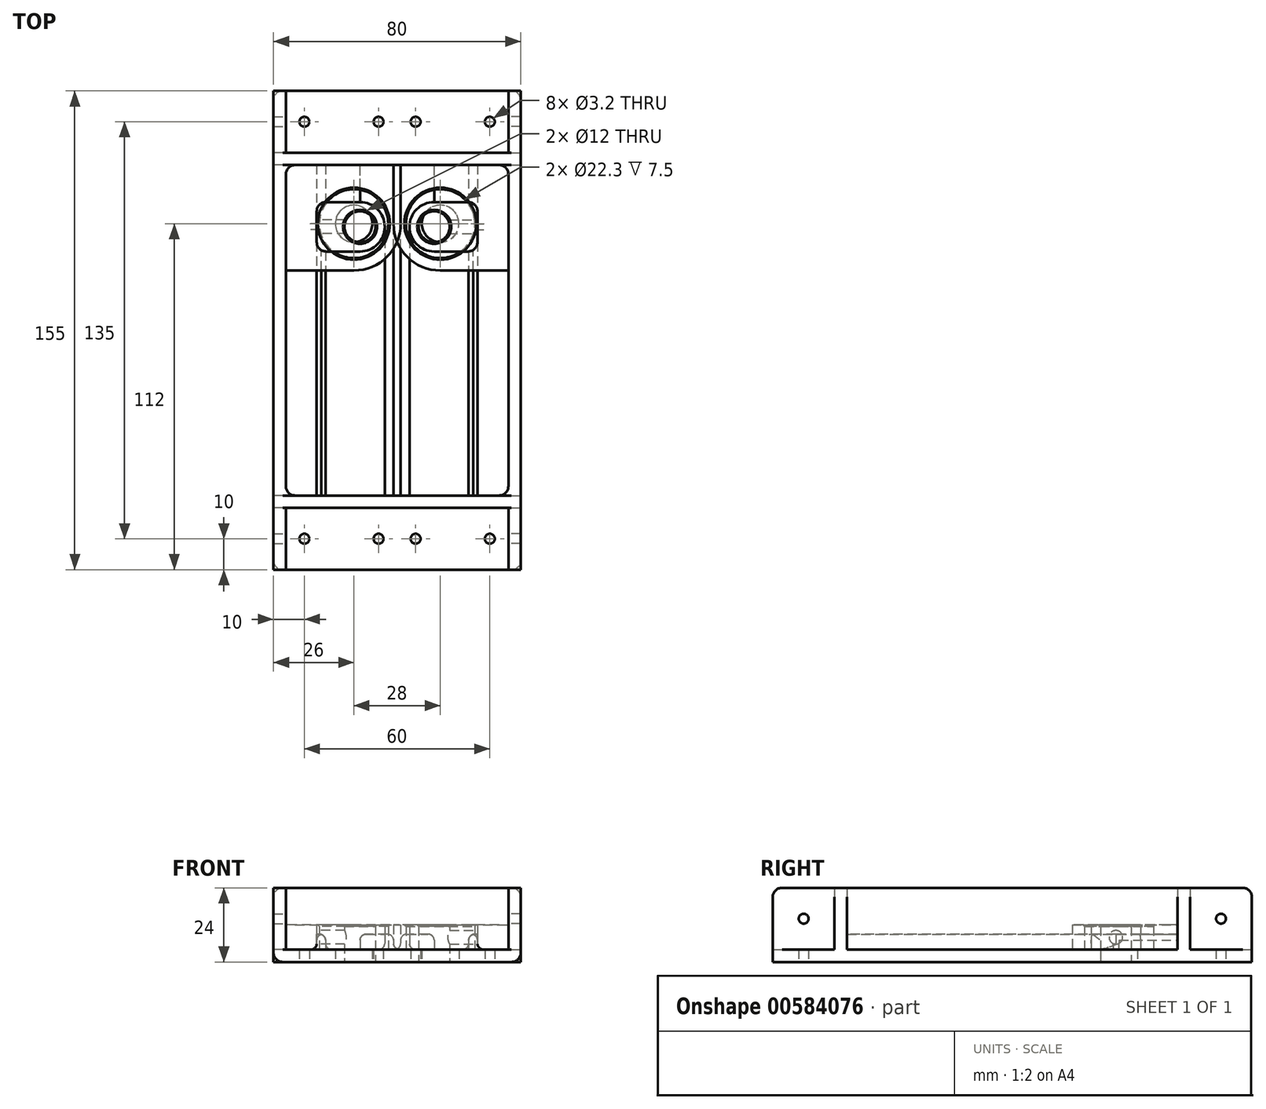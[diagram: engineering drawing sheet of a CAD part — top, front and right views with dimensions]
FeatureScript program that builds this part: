
annotation { "Feature Type Name" : "Feature", "Feature Type Description" : "" }
export const myFeature = defineFeature(function(context is Context, id is Id, definition is map)
    precondition{}
    {
        {
            var Q0;
            Q0=qCreatedBy(makeId("Top.planeOp"),FACE);
            var sketch = newSketch(context, id + "F0", { "sketchPlane" : qUnion([Q0])});
            skLineSegment(sketch, "E0.bottom", {"start": v(40, -77.5) * mm, "end": v(-40, -77.5) * mm});
            skLineSegment(sketch, "E0.top", {"start": v(40, 77.5) * mm, "end": v(-40, 77.5) * mm});
            skLineSegment(sketch, "E0.left", {"start": v(40, -77.5) * mm, "end": v(40, 77.5) * mm});
            skLineSegment(sketch, "E0.right", {"start": v(-40, -77.5) * mm, "end": v(-40, 77.5) * mm});
            skPoint(sketch, "E0.middle", {"position": v(0, 0) * mm});
            skLineSegment(sketch, "E1", {"start": v(-36, 77.5) * mm, "end": v(-36, 57.5) * mm});
            skLineSegment(sketch, "E2", {"start": v(-36, -53.5) * mm, "end": v(40, -53.5) * mm});
            skLineSegment(sketch, "E3", {"start": v(-36, -57.5) * mm, "end": v(40, -57.5) * mm});
            skLineSegment(sketch, "E4", {"start": v(-36, 57.5) * mm, "end": v(40, 57.5) * mm});
            skLineSegment(sketch, "E5", {"start": v(-36, 53.5) * mm, "end": v(40, 53.5) * mm});
            skLineSegment(sketch, "E6.trimOffspring", {"start": v(-36, 53.5) * mm, "end": v(-36, -53.5) * mm});
            skLineSegment(sketch, "E7.trimOffspring", {"start": v(-36, -57.5) * mm, "end": v(-36, -77.5) * mm});
            skCircle(sketch, "E8", {"center": v(-6, 67.5) * mm, "radius": 1.6 * mm});
            skCircle(sketch, "E9", {"center": v(30, 67.5) * mm, "radius": 1.6 * mm});
            skCircle(sketch, "E10", {"center": v(-6, -67.5) * mm, "radius": 1.6 * mm});
            skCircle(sketch, "E11", {"center": v(30, -67.5) * mm, "radius": 1.6 * mm});
            skCircle(sketch, "E12", {"center": v(-14, 34.5) * mm, "radius": 4 * mm, "construction": true});
            skCircle(sketch, "E13", {"center": v(12, 33.5) * mm, "radius": 5 * mm});
            skCircle(sketch, "E14.0", {"center": v(-14, 34.5) * mm, "radius": 6 * mm});
            skSolve(sketch);
        }
        {
            var Q0;
            {var subQ1=sQuery(id+"F0.wireOp",EDGE,"E3");Q0=makeQuery(id+"F0.imprint","IMPRINT",FACE,{"disambiguationData":[TD([[makeQuery(id+"F0.imprint","IMPRINT",EDGE,{"derivedFrom":subQ1}),-1.0]])]});}
            var Q1;
            {var subQ1=sQuery(id+"F0.wireOp",EDGE,"E2");Q1=makeQuery(id+"F0.imprint","IMPRINT",FACE,{"disambiguationData":[TD([[makeQuery(id+"F0.imprint","IMPRINT",EDGE,{"derivedFrom":subQ1}),1.0]])]});}
            var Q2;
            {var subQ0=sQuery(id+"F0.wireOp",EDGE,"E1");Q2=makeQuery(id+"F0.imprint","IMPRINT",FACE,{"disambiguationData":[TD([[makeQuery(id+"F0.imprint","IMPRINT",EDGE,{"derivedFrom":subQ0}),1.0]])]});}
            extrude(context, id + "F1", {"entities" : qUnion([Q0, Q1, Q2]), "depth" : 4 * mm, "offsetDistance" : 25 * mm});
        }
        {
            var Q0;
            {var subQ3=sQuery(id+"F0.wireOp",EDGE,"E0.right");Q0=makeQuery(id+"F0.imprint","IMPRINT",FACE,{"disambiguationData":[TD([[makeQuery(id+"F0.imprint","IMPRINT",EDGE,{"derivedFrom":subQ3}),-1.0]])]});}
            extrude(context, id + "F2", {"entities" : qUnion([Q0]), "operationType" : NewBodyOperationType.ADD, "depth" : 24 * mm, "offsetDistance" : 25 * mm});
        }
        {
            var Q0;
            Q0=makeQuery(id+"F1.opExtrude","CAP_FACE",FACE,{"disambiguationData":[OSD([sQuery(id+"F0.wireOp",EDGE,"E0.left"),sQuery(id+"F0.wireOp",EDGE,"E2"),sQuery(id+"F0.wireOp",EDGE,"E5"),sQuery(id+"F0.wireOp",EDGE,"E6.trimOffspring"),sQuery(id+"F0.wireOp",EDGE,"E13"),sQuery(id+"F0.wireOp",EDGE,"E14.0")])],"isStart":false});
            var sketch = newSketch(context, id + "F3", { "sketchPlane" : qUnion([Q0])});
            skCircle(sketch, "E15", {"center": v(-14, 34.5) * mm, "radius": 11.15 * mm});
            skCircle(sketch, "E16", {"center": v(-14, 34.5) * mm, "radius": 15.15 * mm});
            skCircle(sketch, "E17.0", {"center": v(12, 33.5) * mm, "radius": 8 * mm});
            skLineSegment(sketch, "E18", {"start": v(12, 41.5) * mm, "end": v(26, 41.5) * mm});
            skLineSegment(sketch, "E19", {"start": v(12, 25.5) * mm, "end": v(26, 25.5) * mm});
            skLineSegment(sketch, "E20", {"start": v(26, 41.5) * mm, "end": v(26, 25.5) * mm});
            skLineSegment(sketch, "E21", {"start": v(1.15, 34.5) * mm, "end": v(1.15, 53.5) * mm});
            skLineSegment(sketch, "E22", {"start": v(-14, 19.35) * mm, "end": v(-36, 19.35) * mm});
            skSolve(sketch);
        }
        {
            var Q0;
            Q0=makeQuery(id+"F3.imprint","IMPRINT",FACE,{"disambiguationData":[TD([[makeQuery(id+"F3.imprint","IMPRINT",EDGE,{"derivedFrom":sQuery(id+"F3.wireOp",EDGE,"E15")}),-1.0]])]});
            var Q1;
            {var subQ0=sQuery(id+"F3.wireOp",EDGE,"E21");Q1=makeQuery(id+"F3.imprint","IMPRINT",FACE,{"disambiguationData":[TD([[makeQuery(id+"F3.imprint","IMPRINT",EDGE,{"derivedFrom":subQ0}),1.0]])]});}
            var Q2;
            {var subQ0=sQuery(id+"F3.wireOp",EDGE,"E22");Q2=makeQuery(id+"F3.imprint","IMPRINT",FACE,{"disambiguationData":[TD([[makeQuery(id+"F3.imprint","IMPRINT",EDGE,{"derivedFrom":subQ0}),-1.0]])]});}
            var Q3;
            {var subQ0=sQuery(id+"F3.wireOp",EDGE,"E18");Q3=makeQuery(id+"F3.imprint","IMPRINT",FACE,{"disambiguationData":[TD([[makeQuery(id+"F3.imprint","IMPRINT",EDGE,{"derivedFrom":subQ0}),-1.0]])]});}
            var Q4;
            Q4=makeQuery(id+"F3.imprint","IMPRINT",FACE,{"disambiguationData":[TD([[makeQuery(id+"F3.imprint","IMPRINT",EDGE,{"derivedFrom":makeQuery(id+"F1.opExtrude","CAP_EDGE",EDGE,{"disambiguationData":[OSD([sQuery(id+"F0.wireOp",EDGE,"E13")])],"isStart":false})}),-1.0]])]});
            var Q5;
            {var subQ0=sQuery(id+"F3.wireOp",EDGE,"E16");var subQ1=makeQuery(id+"F1.opExtrude","CAP_EDGE",EDGE,{"disambiguationData":[OSD([sQuery(id+"F0.wireOp",EDGE,"E5")])],"isStart":false});var subQ2=makeQuery(id+"F3.imprint","INTERSECT",VERTEX,{"disambiguationData":[OD(1.0)],"derivedFrom":[subQ1,subQ0]});Q5=makeQuery(id+"F3.imprint","IMPRINT",FACE,{"disambiguationData":[TD([[makeQuery(id+"F3.imprint","IMPRINT",EDGE,{"disambiguationData":[TD([[subQ2,-1.0]])],"derivedFrom":subQ0}),-1.0]])]});}
            extrude(context, id + "F4", {"entities" : qUnion([Q0, Q1, Q2, Q3, Q4, Q5]), "operationType" : NewBodyOperationType.ADD, "depth" : 8 * mm, "offsetDistance" : 25 * mm});
        }
        {
            var Q0;
            Q0=makeQuery(id+"F2.opExtrude","SWEPT_FACE",FACE,{"disambiguationData":[OSD([sQuery(id+"F0.wireOp",EDGE,"E1")])]});
            var sketch = newSketch(context, id + "F5", { "sketchPlane" : qUnion([Q0])});
            skLineSegment(sketch, "E23.0.0", {"start": v(-77.5, 4) * mm, "end": v(-57.5, 4) * mm});
            skLineSegment(sketch, "E23.0.1", {"start": v(-57.5, 4) * mm, "end": v(-57.5, 24) * mm});
            skLineSegment(sketch, "E23.0.2", {"start": v(-57.5, 24) * mm, "end": v(-77.5, 24) * mm});
            skLineSegment(sketch, "E23.0.3", {"start": v(-77.5, 24) * mm, "end": v(-77.5, 4) * mm});
            skCircle(sketch, "E24", {"center": v(67.5, 14) * mm, "radius": 1.6 * mm});
            skPoint(sketch, "E24.centerSnap0", {"position": v(57.5, 14) * mm});
            skPoint(sketch, "E24.centerSnap1", {"position": v(67.5, 4) * mm});
            skCircle(sketch, "E25", {"center": v(-67.5, 14) * mm, "radius": 1.6 * mm});
            skPoint(sketch, "E25.centerSnap0", {"position": v(-77.5, 14) * mm});
            skPoint(sketch, "E25.centerSnap1", {"position": v(-67.5, 4) * mm});
            skSolve(sketch);
        }
        {
            var Q0;
            Q0=makeQuery(id+"F5.imprint","IMPRINT",FACE,{"disambiguationData":[TD([[makeQuery(id+"F5.imprint","IMPRINT",EDGE,{"derivedFrom":sQuery(id+"F5.wireOp",EDGE,"E24")}),1.0]])]});
            var Q1;
            Q1=makeQuery(id+"F5.imprint","IMPRINT",FACE,{"disambiguationData":[TD([[makeQuery(id+"F5.imprint","IMPRINT",EDGE,{"derivedFrom":sQuery(id+"F5.wireOp",EDGE,"E25")}),1.0]])]});
            extrude(context, id + "F6", {"entities" : qUnion([Q0, Q1]), "operationType" : NewBodyOperationType.REMOVE, "endBound" : BoundingType.THROUGH_ALL, "oppositeDirection" : true, "depth" : 25 * mm, "offsetDistance" : 25 * mm});
        }
        {
            var Q0;
            Q0=makeQuery(id+"F4.opExtrude","SWEPT_FACE",FACE,{"disambiguationData":[OSD([sQuery(id+"F3.wireOp",EDGE,"E20")])]});
            var sketch = newSketch(context, id + "F7", { "sketchPlane" : qUnion([Q0])});
            skCircle(sketch, "E26", {"center": v(33.5, 8) * mm, "radius": 2.2 * mm});
            skPoint(sketch, "E26.centerSnap0", {"position": v(41.5, 8) * mm});
            skPoint(sketch, "E26.centerSnap1", {"position": v(33.5, 12) * mm});
            skSolve(sketch);
        }
        {
            var Q0;
            Q0=makeQuery(id+"F7.imprint","IMPRINT",FACE,{"disambiguationData":[TD([[makeQuery(id+"F7.imprint","IMPRINT",EDGE,{"derivedFrom":sQuery(id+"F7.wireOp",EDGE,"E26")}),1.0]])]});
            extrude(context, id + "F8", {"entities" : qUnion([Q0]), "operationType" : NewBodyOperationType.REMOVE, "endBound" : BoundingType.UP_TO_NEXT, "oppositeDirection" : true, "depth" : 25 * mm, "offsetDistance" : 25 * mm});
        }
        {
            var Q0;
            {var subQ0=sQuery(id+"F0.wireOp",EDGE,"E6.trimOffspring");var subQ1=sQuery(id+"F0.wireOp",EDGE,"E5");var subQ2=sQuery(id+"F0.wireOp",EDGE,"E2");var subQ3=sQuery(id+"F0.wireOp",EDGE,"E0.left");Q0=makeQuery(id+"F4.boolean.opBoolean","SPLIT",FACE,{"disambiguationData":[TD([makeQuery(id+"F2.opExtrude","SWEPT_FACE",FACE,{"disambiguationData":[OSD([subQ2])]})])],"derivedFrom":makeQuery(id+"F1.opExtrude","CAP_FACE",FACE,{"disambiguationData":[OSD([subQ3,subQ2,subQ1,subQ0,sQuery(id+"F0.wireOp",EDGE,"E13"),sQuery(id+"F0.wireOp",EDGE,"E14.0")])],"isStart":false})});}
            var sketch = newSketch(context, id + "F9", { "sketchPlane" : qUnion([Q0])});
            skLineSegment(sketch, "E27.left", {"start": v(1.15, 53.5) * mm, "end": v(1.15, -53.5) * mm});
            skLineSegment(sketch, "E28.bottom", {"start": v(26, 53.5) * mm, "end": v(23.15, 53.5) * mm});
            skLineSegment(sketch, "E28.top", {"start": v(26, -53.5) * mm, "end": v(23.15, -53.5) * mm});
            skLineSegment(sketch, "E28.left", {"start": v(26, 53.5) * mm, "end": v(26, -53.5) * mm});
            skLineSegment(sketch, "E28.right", {"start": v(23.15, 53.5) * mm, "end": v(23.15, -53.5) * mm});
            skLineSegment(sketch, "E29", {"start": v(4, 53.5) * mm, "end": v(4, -53.5) * mm});
            skLineSegment(sketch, "E30", {"start": v(1.15, -53.5) * mm, "end": v(4, -53.5) * mm});
            skLineSegment(sketch, "E31", {"start": v(12, 41.5) * mm, "end": v(12, 53.5) * mm});
            skSolve(sketch);
        }
        {
            var Q0;
            {var subQ5=sQuery(id+"F9.wireOp",EDGE,"E31");Q0=makeQuery(id+"F9.imprint","IMPRINT",FACE,{"disambiguationData":[TD([[makeQuery(id+"F9.imprint","IMPRINT",EDGE,{"derivedFrom":subQ5}),1.0]])]});}
            var Q1;
            {var subQ0=sQuery(id+"F9.wireOp",EDGE,"E30");Q1=makeQuery(id+"F9.imprint","IMPRINT",FACE,{"disambiguationData":[TD([[makeQuery(id+"F9.imprint","IMPRINT",EDGE,{"derivedFrom":subQ0}),1.0]])]});}
            var Q2;
            {var subQ0=sQuery(id+"F9.wireOp",EDGE,"E28.bottom");Q2=makeQuery(id+"F9.imprint","IMPRINT",FACE,{"disambiguationData":[TD([[makeQuery(id+"F9.imprint","IMPRINT",EDGE,{"derivedFrom":subQ0}),-1.0]])]});}
            var Q3;
            {var subQ0=sQuery(id+"F9.wireOp",EDGE,"E28.top");Q3=makeQuery(id+"F9.imprint","IMPRINT",FACE,{"disambiguationData":[TD([[makeQuery(id+"F9.imprint","IMPRINT",EDGE,{"derivedFrom":subQ0}),1.0]])]});}
            extrude(context, id + "F10", {"entities" : qUnion([Q0, Q1, Q2, Q3]), "operationType" : NewBodyOperationType.ADD, "depth" : 5 * mm, "offsetDistance" : 25 * mm});
        }
        {
            var Q0;
            {var subQ0=sQuery(id+"F9.wireOp",EDGE,"E28.left");Q0=makeQuery(id+"F10.boolean.opBoolean","MERGE",EDGE,{"derivedFrom":[makeQuery(id+"F4.opExtrude","CAP_EDGE",EDGE,{"disambiguationData":[OSD([sQuery(id+"F3.wireOp",EDGE,"E20")])],"isStart":true}),makeQuery(id+"F10.opExtrude","CAP_EDGE",EDGE,{"disambiguationData":[OSD([subQ0]),TDD([makeQuery(id+"F9.imprint","IMPRINT",EDGE,{"disambiguationData":[TD([[makeQuery(id+"F9.imprint","INTERSECT",VERTEX,{"derivedFrom":[makeQuery(id+"F4.opExtrude","CAP_EDGE",EDGE,{"disambiguationData":[OSD([sQuery(id+"F3.wireOp",EDGE,"E18")])],"isStart":true}),subQ0]}),1.0]])],"derivedFrom":subQ0})])],"isStart":true}),makeQuery(id+"F10.opExtrude","CAP_EDGE",EDGE,{"disambiguationData":[OSD([subQ0]),TDD([makeQuery(id+"F9.imprint","IMPRINT",EDGE,{"disambiguationData":[TD([[makeQuery(id+"F9.imprint","INTERSECT",VERTEX,{"derivedFrom":[makeQuery(id+"F4.opExtrude","CAP_EDGE",EDGE,{"disambiguationData":[OSD([sQuery(id+"F3.wireOp",EDGE,"E19")])],"isStart":true}),subQ0]}),-1.0]])],"derivedFrom":subQ0})])],"isStart":true})]});}
            var Q1;
            {var subQ0=sQuery(id+"F9.wireOp",EDGE,"E28.right");Q1=makeQuery(id+"F10.opExtrude","CAP_EDGE",EDGE,{"disambiguationData":[OSD([subQ0]),TDD([makeQuery(id+"F9.imprint","IMPRINT",EDGE,{"disambiguationData":[TD([[makeQuery(id+"F9.imprint","INTERSECT",VERTEX,{"derivedFrom":[makeQuery(id+"F4.opExtrude","CAP_EDGE",EDGE,{"disambiguationData":[OSD([sQuery(id+"F3.wireOp",EDGE,"E19")])],"isStart":true}),subQ0]}),-1.0]])],"derivedFrom":subQ0})])],"isStart":true});}
            var Q2;
            {var subQ0=sQuery(id+"F9.wireOp",EDGE,"E28.right");Q2=makeQuery(id+"F10.opExtrude","CAP_EDGE",EDGE,{"disambiguationData":[OSD([subQ0]),TDD([makeQuery(id+"F9.imprint","IMPRINT",EDGE,{"disambiguationData":[TD([[makeQuery(id+"F9.imprint","INTERSECT",VERTEX,{"derivedFrom":[makeQuery(id+"F4.opExtrude","CAP_EDGE",EDGE,{"disambiguationData":[OSD([sQuery(id+"F3.wireOp",EDGE,"E18")])],"isStart":true}),subQ0]}),1.0]])],"derivedFrom":subQ0})])],"isStart":true});}
            var Q3;
            Q3=makeQuery(id+"F10.opExtrude","CAP_EDGE",EDGE,{"disambiguationData":[OSD([sQuery(id+"F9.wireOp",EDGE,"E31")])],"isStart":true});
            var Q4;
            Q4=makeQuery(id+"F10.opExtrude","CAP_EDGE",EDGE,{"disambiguationData":[OSD([sQuery(id+"F9.wireOp",EDGE,"E29")])],"isStart":true});
            var Q5;
            Q5=makeQuery(id+"F10.opExtrude","CAP_EDGE",EDGE,{"disambiguationData":[OSD([sQuery(id+"F9.wireOp",EDGE,"E27.left")])],"isStart":true});
            var Q6;
            {var subQ0=sQuery(id+"F9.wireOp",EDGE,"E27.left");Q6=makeQuery(id+"F10.boolean.opBoolean","SPLIT",EDGE,{"disambiguationData":[topologyDisambiguationEdgeConnected([makeQuery(id+"F10.opExtrude","SWEPT_FACE",FACE,{"disambiguationData":[OSD([subQ0])]})])],"derivedFrom":makeQuery(id+"F10.opExtrude","CAP_EDGE",EDGE,{"disambiguationData":[OSD([subQ0])],"isStart":false})});}
            var Q7;
            Q7=makeQuery(id+"F10.opExtrude","CAP_EDGE",EDGE,{"disambiguationData":[OSD([sQuery(id+"F9.wireOp",EDGE,"E31")])],"isStart":false});
            var Q8;
            {var subQ0=sQuery(id+"F9.wireOp",EDGE,"E28.right");Q8=makeQuery(id+"F10.opExtrude","CAP_EDGE",EDGE,{"disambiguationData":[OSD([subQ0]),TDD([makeQuery(id+"F9.imprint","IMPRINT",EDGE,{"disambiguationData":[TD([[makeQuery(id+"F9.imprint","INTERSECT",VERTEX,{"derivedFrom":[makeQuery(id+"F4.opExtrude","CAP_EDGE",EDGE,{"disambiguationData":[OSD([sQuery(id+"F3.wireOp",EDGE,"E18")])],"isStart":true}),subQ0]}),1.0]])],"derivedFrom":subQ0})])],"isStart":false});}
            var Q9;
            {var subQ0=sQuery(id+"F9.wireOp",EDGE,"E28.right");Q9=makeQuery(id+"F10.opExtrude","CAP_EDGE",EDGE,{"disambiguationData":[OSD([subQ0]),TDD([makeQuery(id+"F9.imprint","IMPRINT",EDGE,{"disambiguationData":[TD([[makeQuery(id+"F9.imprint","INTERSECT",VERTEX,{"derivedFrom":[makeQuery(id+"F4.opExtrude","CAP_EDGE",EDGE,{"disambiguationData":[OSD([sQuery(id+"F3.wireOp",EDGE,"E19")])],"isStart":true}),subQ0]}),-1.0]])],"derivedFrom":subQ0})])],"isStart":false});}
            var Q10;
            {var subQ0=sQuery(id+"F9.wireOp",EDGE,"E28.left");Q10=makeQuery(id+"F10.opExtrude","CAP_EDGE",EDGE,{"disambiguationData":[OSD([subQ0]),TDD([makeQuery(id+"F9.imprint","IMPRINT",EDGE,{"disambiguationData":[TD([[makeQuery(id+"F9.imprint","INTERSECT",VERTEX,{"derivedFrom":[makeQuery(id+"F4.opExtrude","CAP_EDGE",EDGE,{"disambiguationData":[OSD([sQuery(id+"F3.wireOp",EDGE,"E19")])],"isStart":true}),subQ0]}),-1.0]])],"derivedFrom":subQ0})])],"isStart":false});}
            fillet(context, id + "F11", {"entities" : qUnion([Q0, Q1, Q2, Q3, Q4, Q5, Q6, Q7, Q8, Q9, Q10]), "radius" : 2 * mm, "tangentPropagation" : true, "allowEdgeOverflow" : false});
        }
        {
            var Q0;
            {var subQ0=sQuery(id+"F0.wireOp",EDGE,"E0.left");Q0=makeQuery(id+"F2.opExtrude","CAP_EDGE",EDGE,{"disambiguationData":[OSD([subQ0]),TDD([makeQuery(id+"F0.imprint","IMPRINT",EDGE,{"disambiguationData":[TD([[makeQuery(id+"F0.imprint","INTERSECT",VERTEX,{"derivedFrom":[subQ0,sQuery(id+"F0.wireOp",EDGE,"E2")]}),1.0]])],"derivedFrom":subQ0})])],"isStart":false});}
            var Q1;
            {var subQ0=sQuery(id+"F0.wireOp",EDGE,"E0.left");Q1=makeQuery(id+"F2.opExtrude","CAP_EDGE",EDGE,{"disambiguationData":[OSD([subQ0]),TDD([makeQuery(id+"F0.imprint","IMPRINT",EDGE,{"disambiguationData":[TD([[makeQuery(id+"F0.imprint","INTERSECT",VERTEX,{"derivedFrom":[subQ0,sQuery(id+"F0.wireOp",EDGE,"E4")]}),1.0]])],"derivedFrom":subQ0})])],"isStart":false});}
            var Q2;
            Q2=makeQuery(id+"F2.opExtrude","CAP_EDGE",EDGE,{"disambiguationData":[OSD([sQuery(id+"F0.wireOp",EDGE,"E0.bottom")])],"isStart":false});
            var Q3;
            Q3=makeQuery(id+"F2.opExtrude","CAP_EDGE",EDGE,{"disambiguationData":[OSD([sQuery(id+"F0.wireOp",EDGE,"E0.top")])],"isStart":false});
            var Q4;
            Q4=makeQuery(id+"F1.opExtrude","SWEPT_EDGE",EDGE,{"disambiguationData":[OSD([sQuery(id+"F0.wireOp",EDGE,"E0.bottom"),sQuery(id+"F0.wireOp",EDGE,"E0.left")])]});
            var Q5;
            Q5=makeQuery(id+"F1.opExtrude","SWEPT_EDGE",EDGE,{"disambiguationData":[OSD([sQuery(id+"F0.wireOp",EDGE,"E0.top"),sQuery(id+"F0.wireOp",EDGE,"E0.left")])]});
            var Q6;
            Q6=makeQuery(id+"F2.opExtrude","CAP_EDGE",EDGE,{"disambiguationData":[OSD([sQuery(id+"F0.wireOp",EDGE,"E0.right")])],"isStart":true});
            var Q7;
            Q7=makeQuery(id+"F4.opExtrude","SWEPT_EDGE",EDGE,{"disambiguationData":[OSD([sQuery(id+"F0.wireOp",EDGE,"E6.trimOffspring"),sQuery(id+"F3.wireOp",EDGE,"E22")])]});
            var Q8;
            Q8=makeQuery(id+"F4.opExtrude","SWEPT_EDGE",EDGE,{"disambiguationData":[OSD([sQuery(id+"F0.wireOp",EDGE,"E5"),sQuery(id+"F3.wireOp",EDGE,"E21")])]});
            var Q9;
            Q9=makeQuery(id+"F4.opExtrude","SWEPT_EDGE",EDGE,{"disambiguationData":[OSD([sQuery(id+"F3.wireOp",EDGE,"E19"),sQuery(id+"F3.wireOp",EDGE,"E20")])]});
            var Q10;
            Q10=makeQuery(id+"F4.opExtrude","SWEPT_EDGE",EDGE,{"disambiguationData":[OSD([sQuery(id+"F3.wireOp",EDGE,"E18"),sQuery(id+"F3.wireOp",EDGE,"E20")])]});
            var Q11;
            Q11=makeQuery(id+"F2.opExtrude","SWEPT_EDGE",EDGE,{"disambiguationData":[OSD([sQuery(id+"F0.wireOp",EDGE,"E5"),sQuery(id+"F0.wireOp",EDGE,"E6.trimOffspring")])]});
            var Q12;
            Q12=makeQuery(id+"F2.opExtrude","SWEPT_EDGE",EDGE,{"disambiguationData":[OSD([sQuery(id+"F0.wireOp",EDGE,"E2"),sQuery(id+"F0.wireOp",EDGE,"E6.trimOffspring")])]});
            var Q13;
            Q13=makeQuery(id+"F1.opExtrude","CAP_EDGE",EDGE,{"disambiguationData":[OSD([sQuery(id+"F0.wireOp",EDGE,"E2")])],"isStart":false});
            var Q14;
            Q14=makeQuery(id+"F1.opExtrude","CAP_EDGE",EDGE,{"disambiguationData":[OSD([sQuery(id+"F0.wireOp",EDGE,"E5")])],"isStart":false});
            var Q15;
            Q15=makeQuery(id+"F1.opExtrude","CAP_EDGE",EDGE,{"disambiguationData":[OSD([sQuery(id+"F0.wireOp",EDGE,"E6.trimOffspring")])],"isStart":false});
            fillet(context, id + "F12", {"entities" : qUnion([Q0, Q1, Q2, Q3, Q4, Q5, Q6, Q7, Q8, Q9, Q10, Q11, Q12, Q13, Q14, Q15]), "radius" : 3 * mm, "tangentPropagation" : true, "allowEdgeOverflow" : false});
        }
        {
            var Q0;
            Q0=makeQuery(id+"F4.opExtrude","CAP_EDGE",EDGE,{"disambiguationData":[OSD([sQuery(id+"F3.wireOp",EDGE,"E15")])],"isStart":false});
            var Q1;
            Q1=makeQuery(id+"F4.opExtrude","CAP_EDGE",EDGE,{"disambiguationData":[OSD([sQuery(id+"F0.wireOp",EDGE,"E13")])],"isStart":false});
            var Q2;
            Q2=makeQuery(id+"F8.boolean.opBoolean","COPY",EDGE,{"derivedFrom":makeQuery(id+"F8.opExtrude","CAP_EDGE",EDGE,{"disambiguationData":[OSD([sQuery(id+"F7.wireOp",EDGE,"E26")])],"isStart":true})});
            chamfer(context, id + "F13", {"entities" : qUnion([Q0, Q1, Q2]), "width" : 0.5 * mm, "tangentPropagation" : true});
        }
        {
            var Q0;
            Q0=makeQuery(id+"F1.opExtrude","SWEPT_BODY",BODY,{"disambiguationData":[OSD([sQuery(id+"F0.wireOp",EDGE,"E0.bottom"),sQuery(id+"F0.wireOp",EDGE,"E0.left"),sQuery(id+"F0.wireOp",EDGE,"E3"),sQuery(id+"F0.wireOp",EDGE,"E7.trimOffspring"),sQuery(id+"F0.wireOp",EDGE,"E10"),sQuery(id+"F0.wireOp",EDGE,"E11")])]});
            var Q1;
            Q1=qCreatedBy(makeId("Right.planeOp"),FACE);
            mirror(context, id + "F14", {"entities" : qUnion([Q0]), "mirrorPlane" : qUnion([Q1])});
        }
    });
